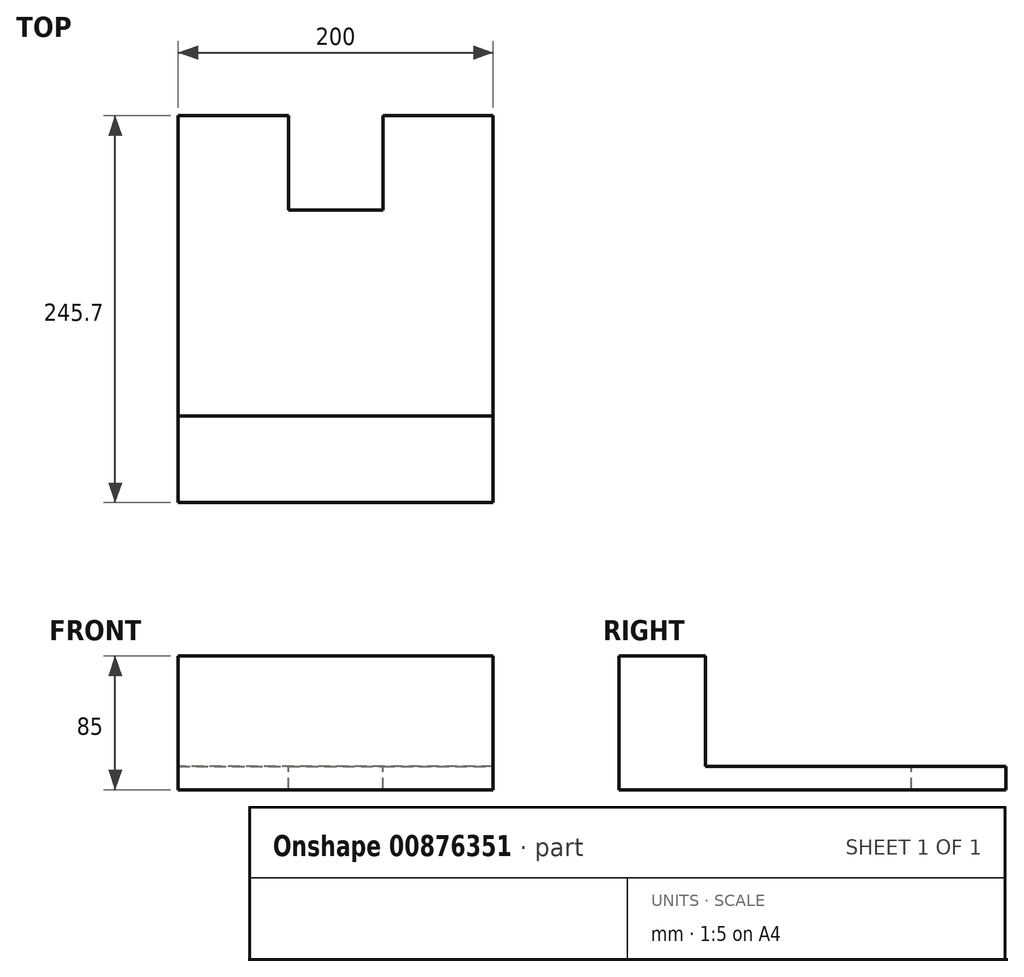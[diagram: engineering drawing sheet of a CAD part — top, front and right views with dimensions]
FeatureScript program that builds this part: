
annotation { "Feature Type Name" : "Feature", "Feature Type Description" : "" }
export const myFeature = defineFeature(function(context is Context, id is Id, definition is map)
    precondition{}
    {
        {
            var Q0;
            Q0=qCreatedBy(makeId("Right.planeOp"),FACE);
            var sketch = newSketch(context, id + "F0", { "sketchPlane" : qUnion([Q0])});
            skLineSegment(sketch, "E0.bottom", {"start": v(27.5, 35) * mm, "end": v(-27.5, 35) * mm});
            skLineSegment(sketch, "E0.top", {"start": v(27.5, -35) * mm, "end": v(-27.5, -35) * mm});
            skLineSegment(sketch, "E0.left", {"start": v(27.5, 35) * mm, "end": v(27.5, -35) * mm});
            skLineSegment(sketch, "E0.right", {"start": v(-27.5, 35) * mm, "end": v(-27.5, -35) * mm});
            skPoint(sketch, "E0.middle", {"position": v(0, 0) * mm});
            skSolve(sketch);
        }
        {
            var Q0;
            Q0=makeQuery(id+"F0.imprint","IMPRINT",FACE,{"disambiguationData":[TD([[makeQuery(id+"F0.imprint","IMPRINT",EDGE,{"derivedFrom":sQuery(id+"F0.wireOp",EDGE,"E0.bottom")}),1.0]])]});
            extrude(context, id + "F1", {"entities" : qUnion([Q0]), "endBound" : BoundingType.SYMMETRIC, "depth" : 200 * mm, "offsetDistance" : 25 * mm});
        }
        {
            var Q0;
            Q0=makeQuery(id+"F1.opExtrude","SWEPT_FACE",FACE,{"disambiguationData":[OSD([sQuery(id+"F0.wireOp",EDGE,"E0.top")])]});
            var sketch = newSketch(context, id + "F2", { "sketchPlane" : qUnion([Q0])});
            skLineSegment(sketch, "E1.bottom", {"start": v(-100, 27.5) * mm, "end": v(100, 27.5) * mm});
            skLineSegment(sketch, "E1.top", {"start": v(-100, -218.2) * mm, "end": v(100, -218.2) * mm});
            skLineSegment(sketch, "E1.left", {"start": v(-100, 27.5) * mm, "end": v(-100, -218.2) * mm});
            skLineSegment(sketch, "E1.right", {"start": v(100, 27.5) * mm, "end": v(100, -218.2) * mm});
            skSolve(sketch);
        }
        {
            var Q0;
            {var subQ0=sQuery(id+"F2.wireOp",EDGE,"E1.top");Q0=makeQuery(id+"F2.imprint","IMPRINT",FACE,{"disambiguationData":[TD([[makeQuery(id+"F2.imprint","IMPRINT",EDGE,{"derivedFrom":subQ0}),1.0]])]});}
            var Q1;
            {var subQ0=sQuery(id+"F2.wireOp",EDGE,"E1.bottom");Q1=makeQuery(id+"F2.imprint","IMPRINT",FACE,{"disambiguationData":[TD([[makeQuery(id+"F2.imprint","IMPRINT",EDGE,{"derivedFrom":subQ0}),1.0]])]});}
            extrude(context, id + "F3", {"entities" : qUnion([Q0, Q1]), "operationType" : NewBodyOperationType.ADD, "depth" : 15 * mm, "offsetDistance" : 25 * mm});
        }
        {
            var Q0;
            Q0=makeQuery(id+"F3.opExtrude","CAP_FACE",FACE,{"disambiguationData":[OSD([sQuery(id+"F2.wireOp",EDGE,"E1.bottom"),sQuery(id+"F2.wireOp",EDGE,"E1.top"),sQuery(id+"F2.wireOp",EDGE,"E1.left"),sQuery(id+"F2.wireOp",EDGE,"E1.right")])],"isStart":true});
            var sketch = newSketch(context, id + "F4", { "sketchPlane" : qUnion([Q0])});
            skLineSegment(sketch, "E2.bottom", {"start": v(-30, 218.2) * mm, "end": v(30, 218.2) * mm});
            skLineSegment(sketch, "E2.top", {"start": v(-30, 158.2) * mm, "end": v(30, 158.2) * mm});
            skLineSegment(sketch, "E2.left", {"start": v(-30, 218.2) * mm, "end": v(-30, 158.2) * mm});
            skLineSegment(sketch, "E2.right", {"start": v(30, 218.2) * mm, "end": v(30, 158.2) * mm});
            skSolve(sketch);
        }
        {
            var Q0;
            Q0=makeQuery(id+"F4.imprint","IMPRINT",FACE,{"disambiguationData":[TD([[makeQuery(id+"F4.imprint","IMPRINT",EDGE,{"derivedFrom":sQuery(id+"F4.wireOp",EDGE,"E2.bottom")}),-1.0]])]});
            extrude(context, id + "F5", {"entities" : qUnion([Q0]), "operationType" : NewBodyOperationType.REMOVE, "oppositeDirection" : true, "depth" : 25 * mm, "offsetDistance" : 25 * mm});
        }
    });
